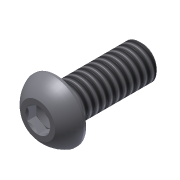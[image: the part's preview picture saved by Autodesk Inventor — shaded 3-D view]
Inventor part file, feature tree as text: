
AUTODESK INVENTOR PART (.ipt)
format: ipt  version: 2013 (Build 170138000, 138)  size: 204,800 bytes
history: native  units: in
note: dims shown in document units (in); Inventor stores cm internally (conversion verified against a paired STEP export)
features: extrude x2, sketch x2, other x1, imported_body x1, thread x1, chamfer x1
ambient origin geometry x8: Origin, YZ Plane, XZ Plane, XY Plane, X Axis, Y Axis, Z Axis, Center Point
feature tree (8):
  parser-record x1  (decoder bookkeeping rows leaked as tree rows — omitted from the tree; the rows remain in map.json)
  imported_body  "Base1"
  extrude  "Extrusion1"  Depth=1.0in TaperAngle=0.0deg
  extrude  "Extrusion2"  Depth=0.625in TaperAngle=0.0deg
  thread  "Thread1"  [1 undecoded]
  chamfer  "Chamfer1"  Distance=0.02in Angle=45.0deg
  sketch  "Sketch1"  dims[d1=0.26in d2=1.0in d3=0.0in]
  sketch  "Sketch2"  dims[d4=0.25in d5=0.625in d6=0.0in d7=1.0in d8=0.0in d9=0.02in d10=0.125in d11=45.0deg]
note: 1 required parameter value undecoded (feature->parameter linkage not recoverable at this tier; creation-order binding heuristic only, values carry confidence <= 0.55)
